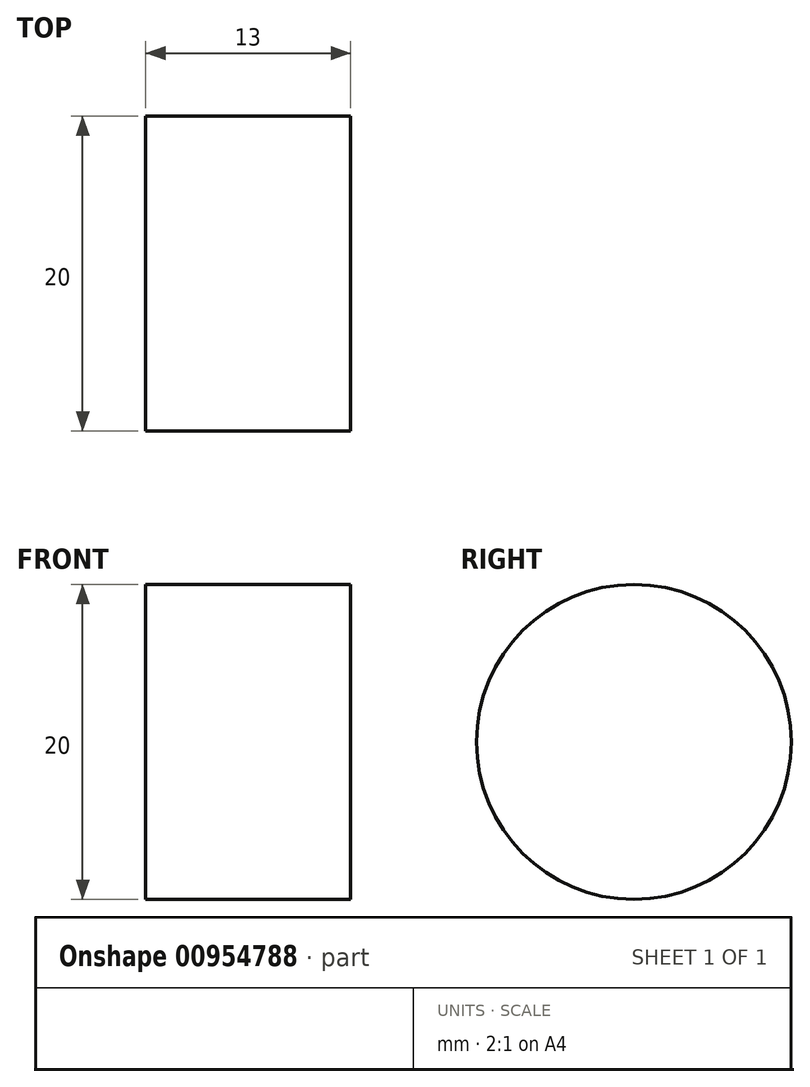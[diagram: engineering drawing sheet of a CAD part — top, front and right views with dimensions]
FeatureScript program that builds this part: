
annotation { "Feature Type Name" : "Feature", "Feature Type Description" : "" }
export const myFeature = defineFeature(function(context is Context, id is Id, definition is map)
    precondition{}
    {
        {
            var Q0;
            Q0=qCreatedBy(makeId("Right.planeOp"),FACE);
            var sketch = newSketch(context, id + "F0", { "sketchPlane" : qUnion([Q0])});
            skCircle(sketch, "E0", {"center": v(0, 0) * mm, "radius": 10 * mm});
            skSolve(sketch);
        }
        {
            var Q0;
            Q0=qSketchRegion(id+"F0",true);
            extrude(context, id + "F1", {"entities" : qUnion([Q0]), "depth" : 13 * mm, "offsetDistance" : 25 * mm, "symmetric" : true});
        }
    });
